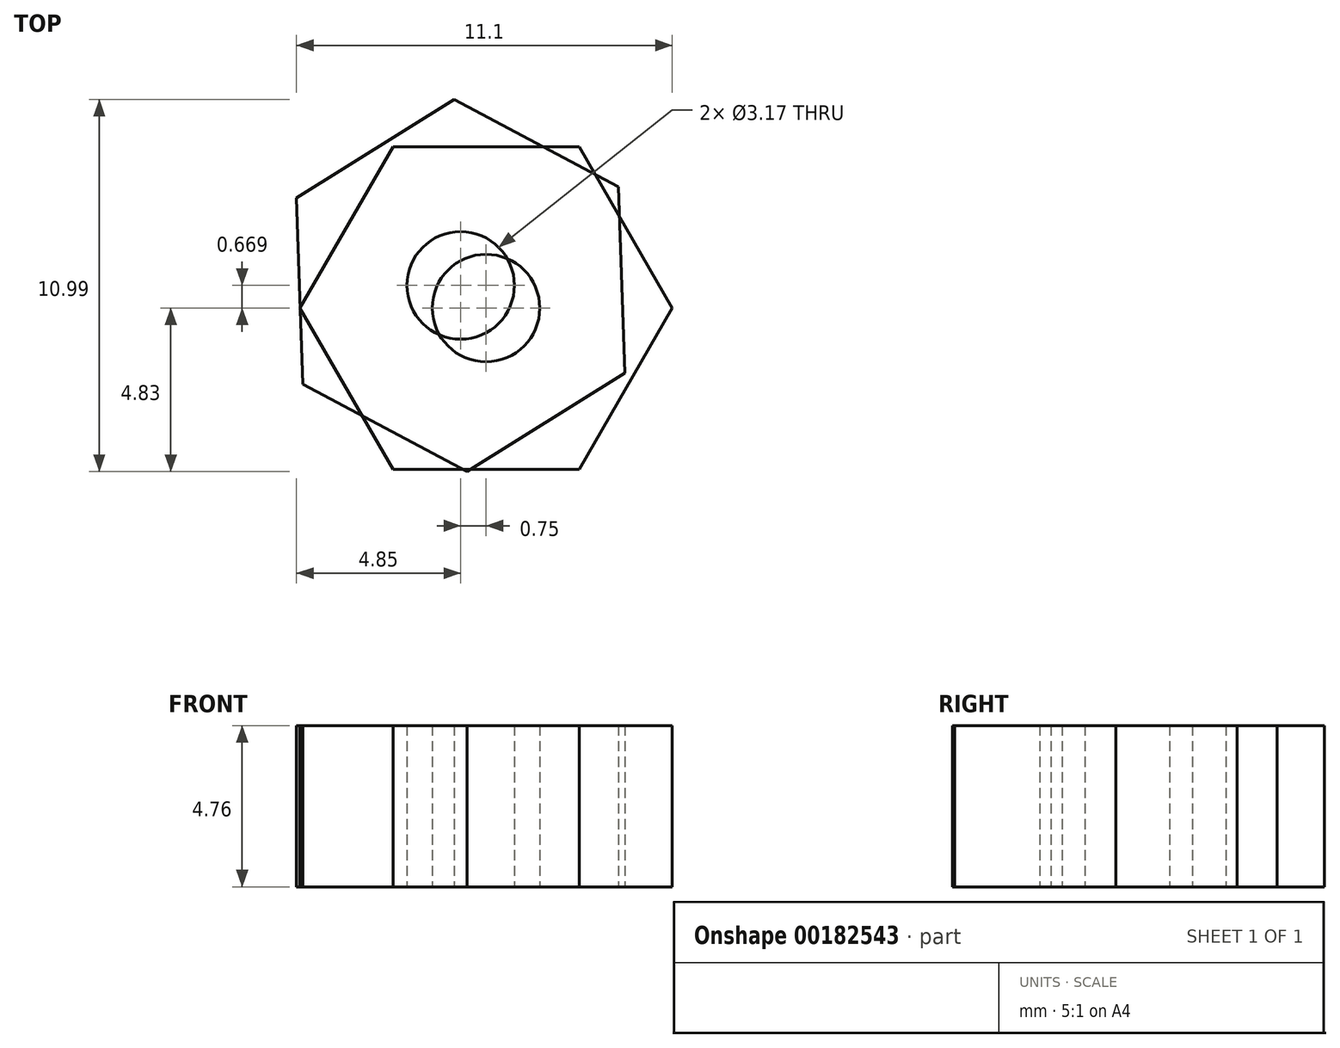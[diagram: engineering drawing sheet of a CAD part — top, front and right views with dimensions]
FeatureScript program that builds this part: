
annotation { "Feature Type Name" : "Feature", "Feature Type Description" : "" }
export const myFeature = defineFeature(function(context is Context, id is Id, definition is map)
    precondition{}
    {
        {
            var Q0;
            Q0=qCreatedBy(makeId("Top.planeOp"),FACE);
            var sketch = newSketch(context, id + "F0", { "sketchPlane" : qUnion([Q0])});
            skCircle(sketch, "E0.cCircle", {"center": v(0, 0.67) * mm, "radius": 4.76 * mm, "construction": true});
            skLineSegment(sketch, "E0.0", {"start": v(-4.85, 3.25) * mm, "end": v(-0.19, 6.16) * mm});
            skLineSegment(sketch, "E0.1", {"start": v(-0.19, 6.16) * mm, "end": v(4.67, 3.58) * mm});
            skLineSegment(sketch, "E0.2", {"start": v(4.67, 3.58) * mm, "end": v(4.85, -1.92) * mm});
            skLineSegment(sketch, "E0.3", {"start": v(4.85, -1.92) * mm, "end": v(0.19, -4.83) * mm});
            skLineSegment(sketch, "E0.4", {"start": v(0.19, -4.83) * mm, "end": v(-4.67, -2.24) * mm});
            skLineSegment(sketch, "E0.5", {"start": v(-4.67, -2.24) * mm, "end": v(-4.85, 3.25) * mm});
            skPoint(sketch, "E0.0.midPoint", {"position": v(-2.52, 4.7) * mm});
            skCircle(sketch, "E1", {"center": v(0, 0.67) * mm, "radius": 1.59 * mm});
            skSolve(sketch);
        }
        {
            var Q0;
            Q0 = qSketchRegion(id + "F0", true);
            extrude(context, id + "F1", {"entities" : qUnion([Q0]), "depth" : 4.76 * mm});
        }
        {
            var Q0;
            Q0=qCreatedBy(makeId("Top.planeOp"),FACE);
            var sketch = newSketch(context, id + "F2", { "sketchPlane" : qUnion([Q0])});
            skCircle(sketch, "E2.cCircle", {"center": v(0.75, 0) * mm, "radius": 4.76 * mm, "construction": true});
            skLineSegment(sketch, "E2.0", {"start": v(3.5, -4.76) * mm, "end": v(-2, -4.76) * mm});
            skLineSegment(sketch, "E2.1", {"start": v(-2, -4.76) * mm, "end": v(-4.75, 0) * mm});
            skLineSegment(sketch, "E2.2", {"start": v(-4.75, 0) * mm, "end": v(-2, 4.76) * mm});
            skLineSegment(sketch, "E2.3", {"start": v(-2, 4.76) * mm, "end": v(3.5, 4.76) * mm});
            skLineSegment(sketch, "E2.4", {"start": v(3.5, 4.76) * mm, "end": v(6.25, 0) * mm});
            skLineSegment(sketch, "E2.5", {"start": v(6.25, 0) * mm, "end": v(3.5, -4.76) * mm});
            skPoint(sketch, "E2.0.midPoint", {"position": v(0.75, -4.76) * mm});
            skCircle(sketch, "E3", {"center": v(0.75, 0) * mm, "radius": 1.59 * mm});
            skSolve(sketch);
        }
        {
            var Q0;
            Q0=makeQuery(id+"F2.imprint","IMPRINT",FACE,{"disambiguationData":[TD([[makeQuery(id+"F2.imprint","IMPRINT",EDGE,{"derivedFrom":sQuery(id+"F2.wireOp",EDGE,"E2.0")}),-1.0]])]});
            extrude(context, id + "F3", {"entities" : qUnion([Q0]), "depth" : 4.76 * mm});
        }
    });
